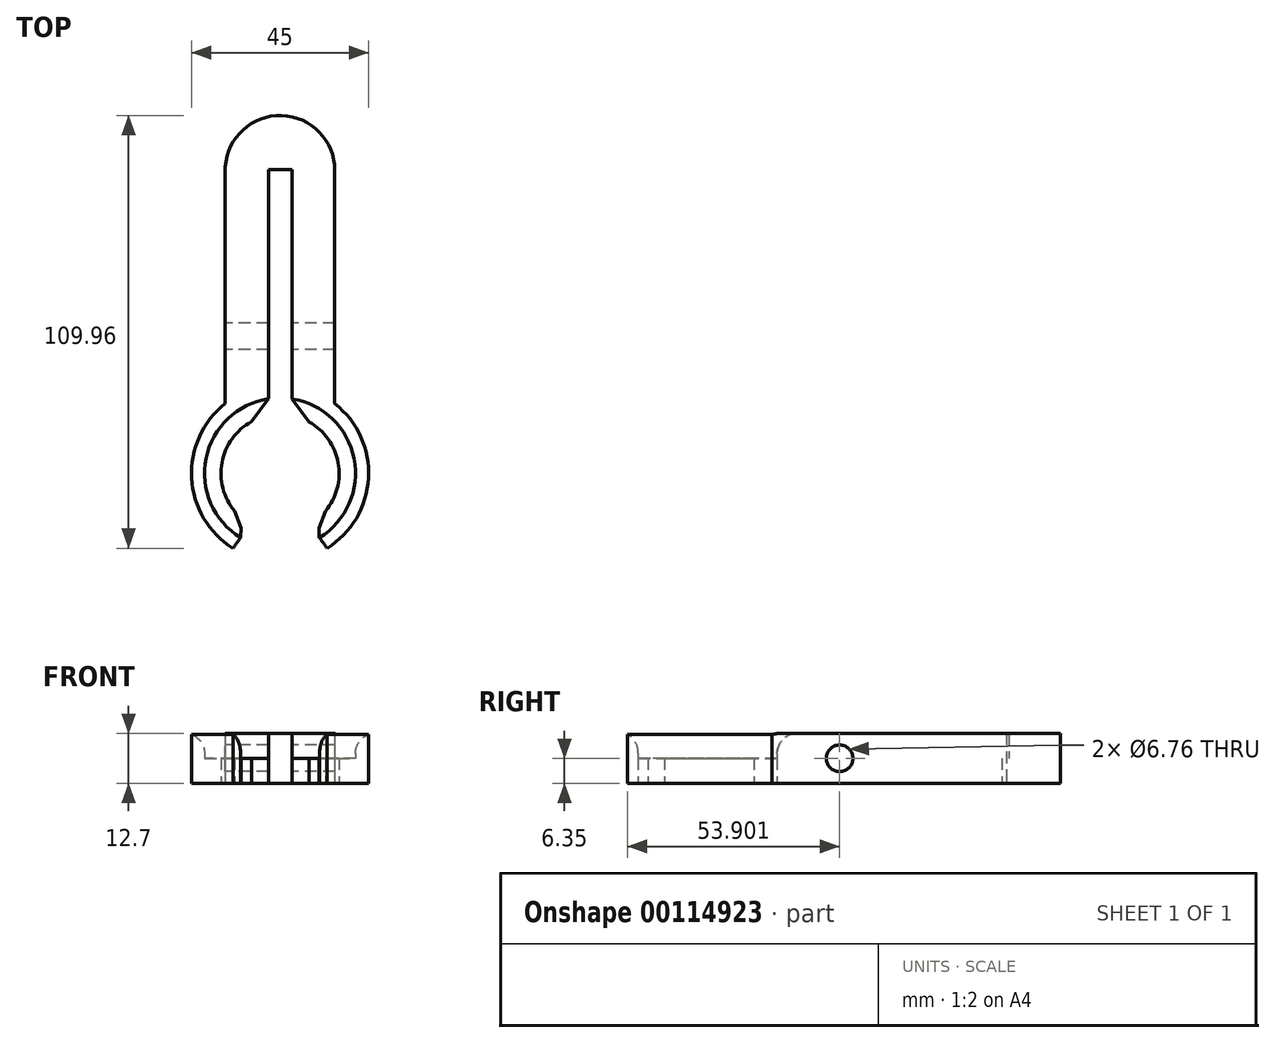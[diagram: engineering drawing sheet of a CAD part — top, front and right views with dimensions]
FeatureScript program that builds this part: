
annotation { "Feature Type Name" : "Feature", "Feature Type Description" : "" }
export const myFeature = defineFeature(function(context is Context, id is Id, definition is map)
    precondition{}
    {
        {
            var Q0;
            Q0=qCreatedBy(makeId("Top.planeOp"),FACE);
            var sketch = newSketch(context, id + "F0", { "sketchPlane" : qUnion([Q0])});
            skArc(sketch, "E0", {"start": v(-13.9, 17.7) * mm, "mid": v(-22.47, -1.2) * mm, "end": v(-11.94, -19.07) * mm});
            skLineSegment(sketch, "E1.left", {"start": v(-13.9, 17.7) * mm, "end": v(-13.9, 77.84) * mm});
            skLineSegment(sketch, "E1.right", {"start": v(13.9, 17.7) * mm, "end": v(13.9, 77) * mm});
            skArc(sketch, "E2", {"start": v(13.9, 76.95) * mm, "mid": v(-0.43, 90.89) * mm, "end": v(-13.9, 76.11) * mm});
            skArc(sketch, "E3", {"start": v(-7.28, 13.12) * mm, "mid": v(-14.75, 2.74) * mm, "end": v(-11.51, -9.62) * mm});
            skLineSegment(sketch, "E4.top", {"start": v(-2.91, 77.14) * mm, "end": v(3.09, 77.14) * mm});
            skLineSegment(sketch, "E4.left", {"start": v(-2.91, 18.96) * mm, "end": v(-2.91, 77.14) * mm});
            skLineSegment(sketch, "E4.right", {"start": v(3.09, 18.93) * mm, "end": v(3.09, 77.14) * mm});
            skPoint(sketch, "E4.bottom.start.orphan", {"position": v(-2.91, 0) * mm});
            skLineSegment(sketch, "E5.left", {"start": v(-9.9, -13.83) * mm, "end": v(-10.05, -16.34) * mm});
            skArc(sketch, "E6.trimOffspring", {"start": v(11.94, -19.07) * mm, "mid": v(22.47, -1.2) * mm, "end": v(13.9, 17.7) * mm});
            skArc(sketch, "E7.trimOffspring", {"start": v(11.51, -9.62) * mm, "mid": v(14.76, 2.68) * mm, "end": v(7.4, 13.05) * mm});
            skLineSegment(sketch, "E8.trimOffspring", {"start": v(9.9, -13.83) * mm, "end": v(9.95, -16.4) * mm});
            skArc(sketch, "E9", {"start": v(9.95, -16.4) * mm, "mid": v(18.83, 3.66) * mm, "end": v(3.09, 18.93) * mm});
            skArc(sketch, "E10.trimOffspring", {"start": v(-2.91, 18.96) * mm, "mid": v(-18.8, 3.8) * mm, "end": v(-10.05, -16.34) * mm});
            skLineSegment(sketch, "E11", {"start": v(-2.91, 18.96) * mm, "end": v(-7.28, 13.12) * mm});
            skLineSegment(sketch, "E12", {"start": v(3.09, 18.93) * mm, "end": v(7.4, 13.05) * mm});
            skLineSegment(sketch, "E13", {"start": v(-11.51, -9.62) * mm, "end": v(-9.9, -13.83) * mm});
            skLineSegment(sketch, "E14", {"start": v(-10.05, -16.34) * mm, "end": v(-11.94, -19.07) * mm});
            skLineSegment(sketch, "E15.MirrorCS", {"start": v(11.51, -9.62) * mm, "end": v(9.9, -13.83) * mm});
            skLineSegment(sketch, "E16.MirrorCS", {"start": v(10.05, -16.34) * mm, "end": v(11.94, -19.07) * mm});
            skSolve(sketch);
        }
        {
            var Q0;
            {var subQ1=sQuery(id+"F0.wireOp",EDGE,"E0");Q0=makeQuery(id+"F0.imprint","IMPRINT",FACE,{"disambiguationData":[TD([[makeQuery(id+"F0.imprint","IMPRINT",EDGE,{"derivedFrom":subQ1}),1.0]])]});}
            extrude(context, id + "F1", {"entities" : qUnion([Q0]), "depth" : 12.7 * mm});
        }
        {
            var Q0;
            Q0 = qSketchRegion(id + "F0", true);
            extrude(context, id + "F2", {"entities" : qUnion([Q0]), "operationType" : NewBodyOperationType.ADD, "depth" : 6.35 * mm});
        }
        {
            var Q0;
            Q0=makeQuery(id+"F1.opExtrude","SWEPT_FACE",FACE,{"disambiguationData":[OSD([sQuery(id+"F0.wireOp",EDGE,"E1.left")])]});
            var sketch = newSketch(context, id + "F3", { "sketchPlane" : qUnion([Q0])});
            skPoint(sketch, "E17", {"position": v(-34.83, 6.35) * mm});
            skSolve(sketch);
        }
        {
            var Q0;
            Q0=sQuery(id+"F3.wireOp",VERTEX,"E17");
            var Q1;
            Q1=makeQuery(id+"F1.opExtrude","SWEPT_BODY",BODY,{"disambiguationData":[OSD([sQuery(id+"F0.wireOp",EDGE,"E0"),sQuery(id+"F0.wireOp",EDGE,"E1.left"),sQuery(id+"F0.wireOp",EDGE,"E1.right"),sQuery(id+"F0.wireOp",EDGE,"E2"),sQuery(id+"F0.wireOp",EDGE,"E4.top"),sQuery(id+"F0.wireOp",EDGE,"E4.left"),sQuery(id+"F0.wireOp",EDGE,"E4.right"),sQuery(id+"F0.wireOp",EDGE,"E5.left"),sQuery(id+"F0.wireOp",EDGE,"E6.trimOffspring"),sQuery(id+"F0.wireOp",EDGE,"E8.trimOffspring"),sQuery(id+"F0.wireOp",EDGE,"E9"),sQuery(id+"F0.wireOp",EDGE,"E10.trimOffspring")])]});
            hole(context, id + "F4", {"style" : HoleStyle.SIMPLE, "endStyle" : HoleEndStyle.THROUGH, "standardTappedOrClearance" : lookupTablePath({ "standard" : "ANSI", "fit" : "Normal (ASME)", "size" : "1/4", "type" : "Clearance" }), "standardBlindInLast" : lookupTablePath({ "fit" : "Free", "standard" : "ANSI", "size" : "1/4", "type" : "Clearance" }), "holeDiameter" : 6.76 * mm, "startFromSketch" : true, "locations" : qUnion([Q0]), "scope" : qUnion([Q1]), "isTappedThrough" : true});
        }
        {
            var Q0;
            Q0=makeQuery(id+"F1.opExtrude","CAP_EDGE",EDGE,{"disambiguationData":[OSD([sQuery(id+"F0.wireOp",EDGE,"E10.trimOffspring")])],"isStart":false});
            var Q1;
            Q1=makeQuery(id+"F1.opExtrude","CAP_EDGE",EDGE,{"disambiguationData":[OSD([sQuery(id+"F0.wireOp",EDGE,"E9")])],"isStart":false});
            fillet(context, id + "F5", {"entities" : qUnion([Q0, Q1]), "radius" : 5.08 * mm, "tangentPropagation" : true, "allowEdgeOverflow" : false});
        }
    });
